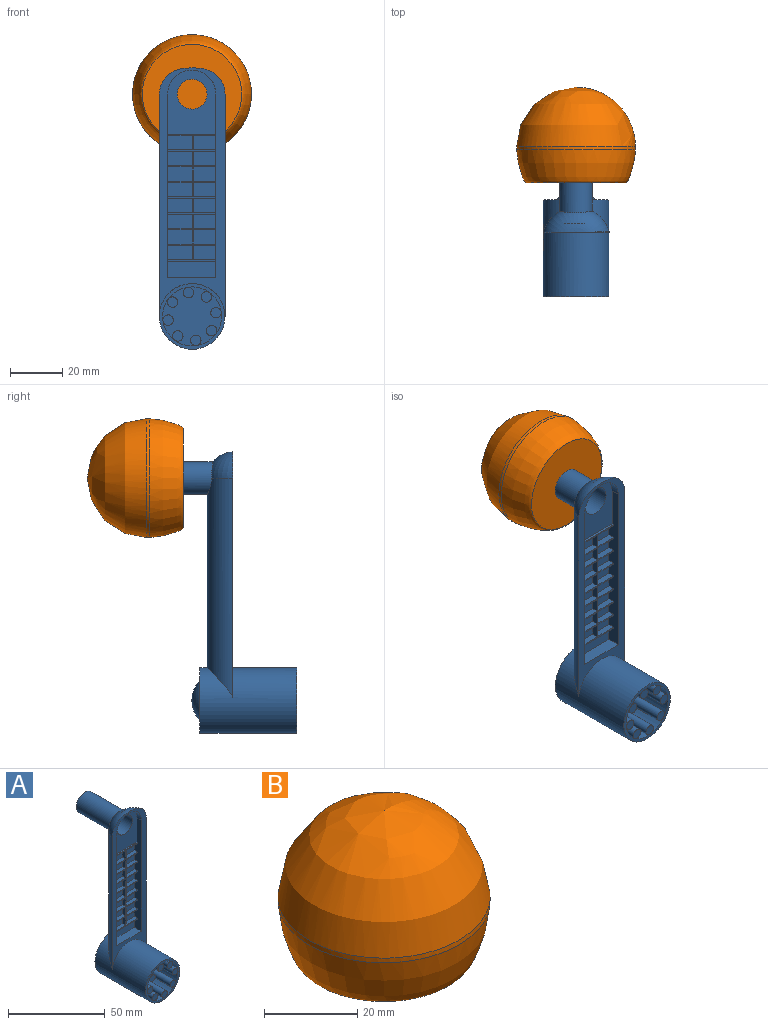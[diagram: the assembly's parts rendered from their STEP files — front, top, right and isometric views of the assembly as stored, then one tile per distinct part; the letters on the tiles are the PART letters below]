
ASSEMBLY  parts=2 mates=1
PART A: 104 faces, bbox 25.4x57.2x107.8 mm
  f0: plane 48.52x18.38mm, normal (0.01,-1,0), area 100mm2, adj f12,f14,f16,f17,f18,f20,f21,f22
  f1: plane 95.04x25.15mm, normal (0.01,-1,0), area 666.8mm2, adj f2,f7,f8,f9,f12,f13,f14,f15
  f2: cylinder r=12.55mm len=37mm, axis (0,1,0), area 2699.6mm2, adj f1,f3,f4,f7,f8
  f3: plane 25.1x25.1mm, normal (0,-1,0), area 93.7mm2, adj f2,f86
  f4: plane 25.1x25.1mm, normal (0,1,0), area 318.1mm2, adj f2,f6
  f5: plane 0.72x0.72mm, normal (0,1,0), area 0.4mm2, adj f6
  f6: torus R=0.36mm, axis (0,1,0), area 206.4mm2, adj f4,f5
  f7: cylinder r=13mm len=85mm, axis (0,0,-1), area 2524.4mm2, adj f1,f2,f8,f9,f10
  f8: plane 0.19x0.06mm, normal (0,0,-1), area 0mm2, adj f1,f2,f7
  f9: torus R=3mm, axis (0,0,1), area 282.7mm2, adj f1,f7,f10
  f10: cylinder r=6.25mm len=25.05mm, axis (0,-1,0), area 949.9mm2, adj f7,f9,f11
  f11: plane 12.5x12.5mm, normal (0,1,0), area 122.7mm2, adj f10
  f12: plane 70.29x5mm, normal (1,0.01,0), area 313.7mm2, adj f0,f1,f13,f15,f48,f49,f51,f52
  f13: plane 18.43x5.17mm, normal (0,0,1), area 91.9mm2, adj f1,f12,f14,f81
  f14: plane 70.29x5mm, normal (-1,-0.01,0), area 313.7mm2, adj f0,f1,f13,f15,f17,f18,f19,f21
  f15: cylinder r=9.19mm len=18.41mm, axis (0.01,-1,0), area 95.3mm2, adj f1,f12,f14,f83
  f16: plane 5.48x2.5mm, normal (1,0.01,0), area 13.7mm2, adj f0,f17,f18,f19
  f17: plane 8.64x2.58mm, normal (0,0,1), area 21.5mm2, adj f0,f14,f16,f19
  f18: plane 8.64x2.58mm, normal (0,0,-1), area 21.5mm2, adj f0,f14,f16,f19
  f19: plane 8.62x5.48mm, normal (0.01,-1,0), area 47.2mm2, adj f14,f16,f17,f18
  f20: plane 5.48x2.5mm, normal (1,0.01,0), area 13.7mm2, adj f0,f21,f22,f23
  f21: plane 8.64x2.58mm, normal (0,0,1), area 21.5mm2, adj f0,f14,f20,f23
  f22: plane 8.64x2.58mm, normal (0,0,-1), area 21.5mm2, adj f0,f14,f20,f23
  f23: plane 8.62x5.48mm, normal (0.01,-1,0), area 47.2mm2, adj f14,f20,f21,f22
  f24: plane 5.48x2.5mm, normal (1,0.01,0), area 13.7mm2, adj f0,f25,f26,f27
  f25: plane 8.64x2.58mm, normal (0,0,1), area 21.5mm2, adj f0,f14,f24,f27
  f26: plane 8.64x2.58mm, normal (0,0,-1), area 21.5mm2, adj f0,f14,f24,f27
  f27: plane 8.62x5.48mm, normal (0.01,-1,0), area 47.2mm2, adj f14,f24,f25,f26
  f28: plane 5.48x2.5mm, normal (1,0.01,0), area 13.7mm2, adj f0,f29,f30,f31
  f29: plane 8.64x2.58mm, normal (0,0,1), area 21.5mm2, adj f0,f14,f28,f31
  f30: plane 8.64x2.58mm, normal (0,0,-1), area 21.5mm2, adj f0,f14,f28,f31
  f31: plane 8.62x5.48mm, normal (0.01,-1,0), area 47.2mm2, adj f14,f28,f29,f30
  f32: plane 5.48x2.5mm, normal (1,0.01,0), area 13.7mm2, adj f0,f33,f34,f35
  f33: plane 8.64x2.58mm, normal (0,0,1), area 21.5mm2, adj f0,f14,f32,f35
  f34: plane 8.64x2.58mm, normal (0,0,-1), area 21.5mm2, adj f0,f14,f32,f35
  f35: plane 8.62x5.48mm, normal (0.01,-1,0), area 47.2mm2, adj f14,f32,f33,f34
  f36: plane 5.48x2.5mm, normal (1,0.01,0), area 13.7mm2, adj f0,f37,f38,f39
  f37: plane 8.64x2.58mm, normal (0,0,1), area 21.5mm2, adj f0,f14,f36,f39
  f38: plane 8.64x2.58mm, normal (0,0,-1), area 21.5mm2, adj f0,f14,f36,f39
  f39: plane 8.62x5.48mm, normal (0.01,-1,0), area 47.2mm2, adj f14,f36,f37,f38
  f40: plane 5.48x2.5mm, normal (1,0.01,0), area 13.7mm2, adj f0,f41,f42,f43
  f41: plane 8.64x2.58mm, normal (0,0,1), area 21.5mm2, adj f0,f14,f40,f43
  f42: plane 8.64x2.58mm, normal (0,0,-1), area 21.5mm2, adj f0,f14,f40,f43
  f43: plane 8.62x5.48mm, normal (0.01,-1,0), area 47.2mm2, adj f14,f40,f41,f42
  f44: plane 5.48x2.5mm, normal (1,0.01,0), area 13.7mm2, adj f0,f45,f46,f47
  f45: plane 8.64x2.58mm, normal (0,0,1), area 21.5mm2, adj f0,f14,f44,f47
  f46: plane 8.64x2.58mm, normal (0,0,-1), area 21.5mm2, adj f0,f14,f44,f47
  f47: plane 8.62x5.48mm, normal (0.01,-1,0), area 47.2mm2, adj f14,f44,f45,f46
  f48: plane 9.47x2.59mm, normal (0,0,-1), area 23.6mm2, adj f0,f12,f50,f51
  f49: plane 9.47x2.59mm, normal (0,0,1), area 23.6mm2, adj f0,f12,f50,f51
  f50: plane 5.48x2.5mm, normal (-1,-0.01,0), area 13.7mm2, adj f0,f48,f49,f51
  f51: plane 9.45x5.48mm, normal (0.01,-1,0), area 51.8mm2, adj f12,f48,f49,f50
  f52: plane 9.47x2.59mm, normal (0,0,-1), area 23.6mm2, adj f0,f12,f54,f55
  f53: plane 9.47x2.59mm, normal (0,0,1), area 23.6mm2, adj f0,f12,f54,f55
  f54: plane 5.48x2.5mm, normal (-1,-0.01,0), area 13.7mm2, adj f0,f52,f53,f55
  f55: plane 9.45x5.48mm, normal (0.01,-1,0), area 51.8mm2, adj f12,f52,f53,f54
  f56: plane 9.47x2.59mm, normal (0,0,-1), area 23.6mm2, adj f0,f12,f58,f59
  f57: plane 9.47x2.59mm, normal (0,0,1), area 23.6mm2, adj f0,f12,f58,f59
  f58: plane 5.48x2.5mm, normal (-1,-0.01,0), area 13.7mm2, adj f0,f56,f57,f59
  f59: plane 9.45x5.48mm, normal (0.01,-1,0), area 51.8mm2, adj f12,f56,f57,f58
  f60: plane 9.47x2.59mm, normal (0,0,-1), area 23.6mm2, adj f0,f12,f62,f63
  f61: plane 9.47x2.59mm, normal (0,0,1), area 23.6mm2, adj f0,f12,f62,f63
  f62: plane 5.48x2.5mm, normal (-1,-0.01,0), area 13.7mm2, adj f0,f60,f61,f63
  f63: plane 9.45x5.48mm, normal (0.01,-1,0), area 51.8mm2, adj f12,f60,f61,f62
  f64: plane 9.47x2.59mm, normal (0,0,-1), area 23.6mm2, adj f0,f12,f66,f67
  f65: plane 9.47x2.59mm, normal (0,0,1), area 23.6mm2, adj f0,f12,f66,f67
  f66: plane 5.48x2.5mm, normal (-1,-0.01,0), area 13.7mm2, adj f0,f64,f65,f67
  f67: plane 9.45x5.48mm, normal (0.01,-1,0), area 51.8mm2, adj f12,f64,f65,f66
  f68: plane 9.47x2.59mm, normal (0,0,-1), area 23.6mm2, adj f0,f12,f70,f71
  f69: plane 9.47x2.59mm, normal (0,0,1), area 23.6mm2, adj f0,f12,f70,f71
  f70: plane 5.48x2.5mm, normal (-1,-0.01,0), area 13.7mm2, adj f0,f68,f69,f71
  f71: plane 9.45x5.48mm, normal (0.01,-1,0), area 51.8mm2, adj f12,f68,f69,f70
  f72: plane 9.47x2.59mm, normal (0,0,-1), area 23.6mm2, adj f0,f12,f74,f75
  f73: plane 9.47x2.59mm, normal (0,0,1), area 23.6mm2, adj f0,f12,f74,f75
  f74: plane 5.48x2.5mm, normal (-1,-0.01,0), area 13.7mm2, adj f0,f72,f73,f75
  f75: plane 9.45x5.48mm, normal (0.01,-1,0), area 51.8mm2, adj f12,f72,f73,f74
  f76: plane 9.47x2.59mm, normal (0,0,-1), area 23.6mm2, adj f0,f12,f78,f79
  f77: plane 9.47x2.59mm, normal (0,0,1), area 23.6mm2, adj f0,f12,f78,f79
  f78: plane 5.48x2.5mm, normal (-1,-0.01,0), area 13.7mm2, adj f0,f76,f77,f79
  f79: plane 9.45x5.48mm, normal (0.01,-1,0), area 51.8mm2, adj f12,f76,f77,f78
  f80: plane 18.4x2.67mm, normal (0,0,-1), area 45.9mm2, adj f0,f12,f14,f81
  f81: plane 18.38x6.45mm, normal (0.01,-1,0), area 118.5mm2, adj f12,f13,f14,f80
  f82: plane 18.39x0.97mm, normal (0,0,1), area 14.7mm2, adj f0,f12,f14,f83
  f83: plane 24.72x18.59mm, normal (0.01,-1,0), area 311.9mm2, adj f12,f14,f15,f82,f84
  f84: cylinder r=5.71mm len=27.21mm, axis (0,-1,0), area 975.9mm2, adj f83,f85
  f85: plane 11.42x11.42mm, normal (0,-1,0), area 102.3mm2, adj f84
  f86: cylinder r=11.3mm len=32.8mm, axis (0,-1,0), area 2328.8mm2, adj f3,f87
  f87: plane 22.6x22.6mm, normal (0,-1,0), area 300.6mm2, adj f86,f88,f90,f92,f94,f96,f98,f100
  f88: cylinder r=2mm len=32.8mm, axis (0,1,0), area 412.2mm2, adj f87,f89
  f89: plane 4x4mm, normal (0,-1,0), area 12.6mm2, adj f88
  f90: cylinder r=2mm len=32.8mm, axis (0,1,0), area 412.2mm2, adj f87,f91
  f91: plane 4x4mm, normal (0,-1,0), area 12.6mm2, adj f90
  f92: cylinder r=2mm len=32.8mm, axis (0,1,0), area 412.2mm2, adj f87,f93
  f93: plane 4x4mm, normal (0,-1,0), area 12.6mm2, adj f92
  f94: cylinder r=2mm len=32.8mm, axis (0,1,0), area 412.2mm2, adj f87,f95
  f95: plane 4x4mm, normal (0,-1,0), area 12.6mm2, adj f94
  f96: cylinder r=2mm len=32.8mm, axis (0,1,0), area 412.2mm2, adj f87,f97
  f97: plane 4x4mm, normal (0,-1,0), area 12.6mm2, adj f96
  f98: cylinder r=2mm len=32.8mm, axis (0,1,0), area 412.2mm2, adj f87,f99
  f99: plane 4x4mm, normal (0,-1,0), area 12.6mm2, adj f98
  f100: cylinder r=2mm len=32.8mm, axis (0,1,0), area 412.2mm2, adj f87,f101
  f101: plane 4x4mm, normal (0,-1,0), area 12.6mm2, adj f100
  f102: cylinder r=2mm len=32.8mm, axis (0,1,0), area 412.2mm2, adj f87,f103
  f103: plane 4x4mm, normal (0,-1,0), area 12.6mm2, adj f102
PART B: 7 faces, bbox 45.4x45.4x36.6 mm
  f0: plane 38x38mm, normal (0,0,-1), area 1011.3mm2, adj f1,f5
  f1: bspline ~45.4x45.4mm, area 1818.5mm2, adj f0,f3
  f2: plane 0.06x0.06mm, normal (0,0,1), area 0mm2, adj f4
  f3: extruded ~45.4x45.4mm, area 175.4mm2, adj f1,f4
  f4: bspline ~45.39x45.36mm, area 3235.8mm2, adj f2,f3
  f5: cylinder r=6.25mm len=12.5mm, axis (0,0,-1), area 392.7mm2, adj f0,f6
  f6: plane 12.5x12.5mm, normal (0,0,-1), area 122.7mm2, adj f5
PLACE A t=(-3.15,-32.5,-63.28)mm
PLACE B rot(axis=(-1,0,0),90deg) t=(-3.19,-26.1,21.72)mm
MATE revolute B.f5 <-> A.f10  axis (0,-1,0) through (-3.19,-26.1,21.72)mm
